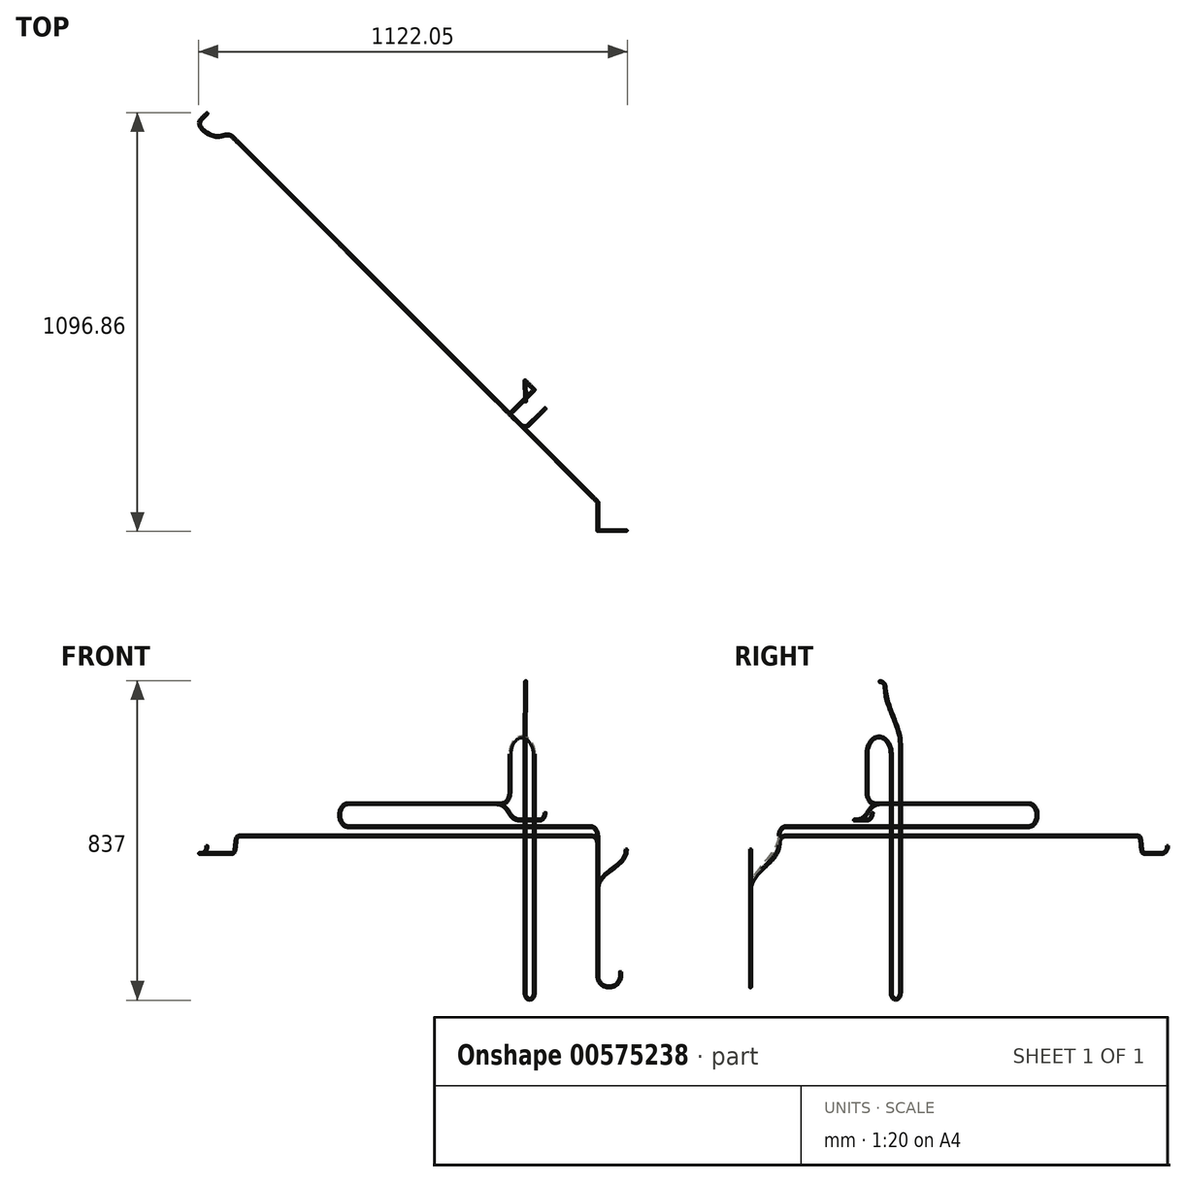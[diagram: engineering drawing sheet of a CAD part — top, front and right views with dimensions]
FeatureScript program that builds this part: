
annotation { "Feature Type Name" : "Feature", "Feature Type Description" : "" }
export const myFeature = defineFeature(function(context is Context, id is Id, definition is map)
    precondition{}
    {
        {
            var Q0;
            Q0=qCreatedBy(makeId("Top.planeOp"),FACE);
            var sketch = newSketch(context, id + "F0", { "sketchPlane" : qUnion([Q0])});
            skCircle(sketch, "E0", {"center": v(0, 0) * mm, "radius": 2.5 * mm});
            skSolve(sketch);
        }
        {
            var Q0;
            Q0=qCreatedBy(makeId("Front.planeOp"),FACE);
            var sketch = newSketch(context, id + "F1", { "sketchPlane" : qUnion([Q0])});
            skLineSegment(sketch, "E1", {"start": v(0, 0) * mm, "end": v(0, -10) * mm});
            skArc(sketch, "E2", {"start": v(-60, -10) * mm, "mid": v(-30, -40) * mm, "end": v(0, -10) * mm});
            skLineSegment(sketch, "E3", {"start": v(-60, -10) * mm, "end": v(-60, 215) * mm});
            skFitSpline(sketch, "E4", {"points": [v(-60, 215) * mm, v(-22.5, 268) * mm, v(15, 321) * mm], "startDerivative": vector(0, 150) * mm, "endDerivative": vector(0, 150) * mm});
            skLineSegment(sketch, "E5", {"start": v(15, 296) * mm, "end": v(15, 321) * mm, "construction": true});
            skLineSegment(sketch, "E6", {"start": v(-60, 240) * mm, "end": v(-60, 215) * mm, "construction": true});
            skLineSegment(sketch, "E7", {"start": v(15, 321) * mm, "end": v(-60, 215) * mm, "construction": true});
            skSolve(sketch);
        }
        {
            var Q0;
            Q0=qSketchRegion(id+"F0",true);
            var Q1;
            Q1=qConstructionFilter(qBodyType(qCreatedBy(id+"F1",EDGE),BodyType.WIRE),ConstructionObject.NO);
            sweep(context, id + "F2", {"profiles" : qUnion([Q0]), "path" : qUnion([Q1])});
        }
        {
            var Q0;
            Q0=qCreatedBy(makeId("Front.planeOp"),FACE);
            var sketch = newSketch(context, id + "F3", { "sketchPlane" : qUnion([Q0])});
            skLineSegment(sketch, "E8", {"start": v(0, 0) * mm, "end": v(0, -10) * mm});
            skArc(sketch, "E9", {"start": v(-60, -10) * mm, "mid": v(-30, -40) * mm, "end": v(0, -10) * mm});
            skLineSegment(sketch, "E10", {"start": v(-60, -10) * mm, "end": v(-60, 215) * mm});
            skSolve(sketch);
        }
        {
            var Q0;
            Q0=qCreatedBy(makeId("Right.planeOp"),FACE);
            var Q1;
            Q1=sQuery(id+"F3.wireOp",VERTEX,"E10.end");
            cPlane(context, id + "F4", {"entities" : qUnion([Q0, Q1]), "cplaneType" : CPlaneType.PLANE_POINT, "offset" : 25 * mm, "width" : 150 * mm, "height" : 150 * mm});
        }
        {
            var Q0;
            Q0=qCreatedBy(id+"F4.planeOp",FACE);
            var sketch = newSketch(context, id + "F5", { "sketchPlane" : qUnion([Q0])});
            skFitSpline(sketch, "E11", {"points": [v(0, 215) * mm, v(37.5, 275) * mm, v(75, 335) * mm], "startDerivative": vector(0, 150) * mm, "endDerivative": vector(0, 150) * mm});
            skLineSegment(sketch, "E12", {"start": v(75, 310) * mm, "end": v(75, 335) * mm, "construction": true});
            skLineSegment(sketch, "E13", {"start": v(0, 240) * mm, "end": v(0, 215) * mm, "construction": true});
            skLineSegment(sketch, "E14", {"start": v(0, 215) * mm, "end": v(75, 335) * mm, "construction": true});
            skSolve(sketch);
        }
        {
            var Q0;
            Q0=sQuery(id+"F5.wireOp",EDGE,"E12");
            cPlane(context, id + "F6", {"entities" : qUnion([Q0]), "cplaneType" : CPlaneType.LINE_ANGLE, "offset" : 25 * mm, "angle" : 135 * degree, "oppositeDirection" : true, "width" : 150 * mm, "height" : 150 * mm});
        }
        {
            var Q0;
            Q0=qCreatedBy(id+"F6.planeOp",FACE);
            var sketch = newSketch(context, id + "F7", { "sketchPlane" : qUnion([Q0])});
            skArc(sketch, "E15", {"start": v(-95.46, 335) * mm, "mid": v(-101.32, 349.14) * mm, "end": v(-115.46, 355) * mm});
            skLineSegment(sketch, "E16", {"start": v(-115.46, 355) * mm, "end": v(-1423.46, 355) * mm});
            skFitSpline(sketch, "E17", {"points": [v(-1423.46, 355) * mm, v(-1435.96, 332.5) * mm, v(-1448.46, 310) * mm], "startDerivative": vector(-60, 0) * mm, "endDerivative": vector(-60, 0) * mm});
            skLineSegment(sketch, "E18", {"start": v(-1433.46, 355) * mm, "end": v(-1423.46, 355) * mm, "construction": true});
            skLineSegment(sketch, "E19", {"start": v(-1438.46, 310) * mm, "end": v(-1448.46, 310) * mm, "construction": true});
            skLineSegment(sketch, "E20", {"start": v(-1448.46, 310) * mm, "end": v(-1423.46, 355) * mm, "construction": true});
            skSolve(sketch);
        }
        {
            var Q0;
            Q0=sQuery(id+"F7.wireOp",EDGE,"E19");
            cPlane(context, id + "F8", {"entities" : qUnion([Q0]), "cplaneType" : CPlaneType.LINE_ANGLE, "offset" : 25 * mm, "angle" : 0 * degree, "width" : 150 * mm, "height" : 150 * mm});
        }
        {
            var Q0;
            Q0=qCreatedBy(id+"F8.planeOp",FACE);
            var sketch = newSketch(context, id + "F9", { "sketchPlane" : qUnion([Q0])});
            skFitSpline(sketch, "E21", {"points": [v(-1016.72, 1031.72) * mm, v(-1061.72, 1032.72) * mm, v(-1096.72, 1077.72) * mm], "startDerivative": vector(-67.63, 67.63) * mm, "endDerivative": vector(100.16, 100.16) * mm});
            skLineSegment(sketch, "E22", {"start": v(-1114.4, 1060.04) * mm, "end": v(-1096.72, 1077.72) * mm, "construction": true});
            skLineSegment(sketch, "E23", {"start": v(-1016.72, 1031.72) * mm, "end": v(-1027.32, 1042.32) * mm, "construction": true});
            skSolve(sketch);
        }
        {
            var Q0;
            Q0=sQuery(id+"F9.wireOp",EDGE,"E22");
            cPlane(context, id + "F10", {"entities" : qUnion([Q0]), "cplaneType" : CPlaneType.LINE_ANGLE, "offset" : 25 * mm, "angle" : 90 * degree, "width" : 150 * mm, "height" : 150 * mm});
        }
        {
            var Q0;
            Q0=qCreatedBy(id+"F10.planeOp",FACE);
            var sketch = newSketch(context, id + "F11", { "sketchPlane" : qUnion([Q0])});
            skArc(sketch, "E24", {"start": v(-13.44, 310) * mm, "mid": v(0.7, 315.86) * mm, "end": v(6.56, 330) * mm});
            skSolve(sketch);
        }
        {
            var Q0;
            Q0=qSketchRegion(id+"F0",true);
            var Q1;
            Q1=qConstructionFilter(qBodyType(qCreatedBy(id+"F3",EDGE),BodyType.WIRE),ConstructionObject.NO);
            var Q2;
            Q2=qConstructionFilter(qBodyType(qCreatedBy(id+"F5",EDGE),BodyType.WIRE),ConstructionObject.NO);
            var Q3;
            Q3=qConstructionFilter(qBodyType(qCreatedBy(id+"F7",EDGE),BodyType.WIRE),ConstructionObject.NO);
            var Q4;
            Q4=qConstructionFilter(qBodyType(qCreatedBy(id+"F9",EDGE),BodyType.WIRE),ConstructionObject.NO);
            var Q5;
            Q5=qConstructionFilter(qBodyType(qCreatedBy(id+"F11",EDGE),BodyType.WIRE),ConstructionObject.NO);
            sweep(context, id + "F12", {"profiles" : qUnion([Q0]), "path" : qUnion([Q1, Q2, Q3, Q4, Q5])});
        }
        {
            var Q0;
            Q0=qCreatedBy(makeId("Front.planeOp"),FACE);
            var sketch = newSketch(context, id + "F13", { "sketchPlane" : qUnion([Q0])});
            skLineSegment(sketch, "E25", {"start": v(0, 0) * mm, "end": v(0, -10) * mm});
            skArc(sketch, "E26", {"start": v(-60, -10) * mm, "mid": v(-30, -40) * mm, "end": v(0, -10) * mm});
            skLineSegment(sketch, "E27", {"start": v(-60, -10) * mm, "end": v(-60, 215) * mm});
            skSolve(sketch);
        }
        {
            var Q0;
            Q0=qCreatedBy(makeId("Right.planeOp"),FACE);
            var Q1;
            Q1=sQuery(id+"F13.wireOp",VERTEX,"E27.end");
            cPlane(context, id + "F14", {"entities" : qUnion([Q0, Q1]), "cplaneType" : CPlaneType.PLANE_POINT, "offset" : 25 * mm, "width" : 150 * mm, "height" : 150 * mm});
        }
        {
            var Q0;
            Q0=qCreatedBy(id+"F14.planeOp",FACE);
            var sketch = newSketch(context, id + "F15", { "sketchPlane" : qUnion([Q0])});
            skFitSpline(sketch, "E28", {"points": [v(0, 215) * mm, v(37.5, 285) * mm, v(75, 355) * mm], "startDerivative": vector(0, 150) * mm, "endDerivative": vector(0, 150) * mm});
            skLineSegment(sketch, "E29", {"start": v(75, 330) * mm, "end": v(75, 355) * mm, "construction": true});
            skLineSegment(sketch, "E30", {"start": v(0, 240) * mm, "end": v(0, 215) * mm, "construction": true});
            skLineSegment(sketch, "E31", {"start": v(0, 215) * mm, "end": v(75, 355) * mm, "construction": true});
            skSolve(sketch);
        }
        {
            var Q0;
            Q0=sQuery(id+"F15.wireOp",EDGE,"E29");
            cPlane(context, id + "F16", {"entities" : qUnion([Q0]), "cplaneType" : CPlaneType.LINE_ANGLE, "offset" : 25 * mm, "angle" : 135 * degree, "oppositeDirection" : true, "width" : 150 * mm, "height" : 150 * mm});
        }
        {
            var Q0;
            Q0=qCreatedBy(id+"F16.planeOp",FACE);
            var sketch = newSketch(context, id + "F17", { "sketchPlane" : qUnion([Q0])});
            skArc(sketch, "E32", {"start": v(-95.46, 355) * mm, "mid": v(-102.78, 372.68) * mm, "end": v(-120.46, 380) * mm});
            skLineSegment(sketch, "E33", {"start": v(-120.46, 380) * mm, "end": v(-1020.46, 380) * mm});
            skArc(sketch, "E34", {"start": v(-1020.46, 440) * mm, "mid": v(-1050.46, 410) * mm, "end": v(-1020.46, 380) * mm});
            skLineSegment(sketch, "E35", {"start": v(-1020.46, 440) * mm, "end": v(-470.46, 440) * mm});
            skFitSpline(sketch, "E36", {"points": [v(-470.46, 440) * mm, v(-425.46, 418.5) * mm, v(-380.46, 397) * mm], "startDerivative": vector(150, 0) * mm, "endDerivative": vector(150, 0) * mm});
            skLineSegment(sketch, "E37", {"start": v(-445.46, 440) * mm, "end": v(-470.46, 440) * mm, "construction": true});
            skLineSegment(sketch, "E38", {"start": v(-405.46, 397) * mm, "end": v(-380.46, 397) * mm, "construction": true});
            skLineSegment(sketch, "E39", {"start": v(-380.46, 397) * mm, "end": v(-470.46, 440) * mm, "construction": true});
            skSolve(sketch);
        }
        {
            var Q0;
            Q0=qCreatedBy(makeId("Top.planeOp"),FACE);
            var Q1;
            Q1=sQuery(id+"F17.wireOp",VERTEX,"E36.end");
            cPlane(context, id + "F18", {"entities" : qUnion([Q0, Q1]), "cplaneType" : CPlaneType.PLANE_POINT, "offset" : 0 * mm, "width" : 150 * mm, "height" : 150 * mm});
        }
        {
            var Q0;
            Q0=qCreatedBy(id+"F18.planeOp",FACE);
            var sketch = newSketch(context, id + "F19", { "sketchPlane" : qUnion([Q0])});
            skArc(sketch, "E40", {"start": v(-261.53, 276.53) * mm, "mid": v(-250.92, 272.13) * mm, "end": v(-240.31, 276.53) * mm});
            skLineSegment(sketch, "E41", {"start": v(-261.53, 276.53) * mm, "end": v(-250.92, 287.13) * mm, "construction": true});
            skLineSegment(sketch, "E42", {"start": v(-240.31, 276.53) * mm, "end": v(-250.92, 287.13) * mm, "construction": true});
            skLineSegment(sketch, "E43", {"start": v(-240.31, 276.53) * mm, "end": v(-212.03, 304.8) * mm});
            skSolve(sketch);
        }
        {
            var Q0;
            Q0=sQuery(id+"F19.wireOp",EDGE,"E43");
            cPlane(context, id + "F20", {"entities" : qUnion([Q0]), "cplaneType" : CPlaneType.LINE_ANGLE, "offset" : 25 * mm, "angle" : 90 * degree, "width" : 150 * mm, "height" : 150 * mm});
        }
        {
            var Q0;
            Q0=qCreatedBy(id+"F20.planeOp",FACE);
            var sketch = newSketch(context, id + "F21", { "sketchPlane" : qUnion([Q0])});
            skArc(sketch, "E44", {"start": v(65.6, 397) * mm, "mid": v(79.75, 402.86) * mm, "end": v(85.6, 417) * mm});
            skSolve(sketch);
        }
        {
            var Q0;
            Q0=qSketchRegion(id+"F0",true);
            var Q1;
            Q1=qConstructionFilter(qBodyType(qCreatedBy(id+"F13",EDGE),BodyType.WIRE),ConstructionObject.NO);
            var Q2;
            Q2=qConstructionFilter(qBodyType(qCreatedBy(id+"F15",EDGE),BodyType.WIRE),ConstructionObject.NO);
            var Q3;
            Q3=qConstructionFilter(qBodyType(qCreatedBy(id+"F17",EDGE),BodyType.WIRE),ConstructionObject.NO);
            var Q4;
            Q4=qConstructionFilter(qBodyType(qCreatedBy(id+"F19",EDGE),BodyType.WIRE),ConstructionObject.NO);
            var Q5;
            Q5=qConstructionFilter(qBodyType(qCreatedBy(id+"F21",EDGE),BodyType.WIRE),ConstructionObject.NO);
            sweep(context, id + "F22", {"profiles" : qUnion([Q0]), "path" : qUnion([Q1, Q2, Q3, Q4, Q5])});
        }
        {
            var Q0;
            Q0=qCreatedBy(makeId("Front.planeOp"),FACE);
            var sketch = newSketch(context, id + "F23", { "sketchPlane" : qUnion([Q0])});
            skLineSegment(sketch, "E45", {"start": v(0, 0) * mm, "end": v(0, -10) * mm});
            skArc(sketch, "E46", {"start": v(-60, -10) * mm, "mid": v(-30, -40) * mm, "end": v(0, -10) * mm});
            skLineSegment(sketch, "E47", {"start": v(-60, -10) * mm, "end": v(-60, 215) * mm});
            skSolve(sketch);
        }
        {
            var Q0;
            Q0=qCreatedBy(makeId("Right.planeOp"),FACE);
            var Q1;
            Q1=sQuery(id+"F23.wireOp",VERTEX,"E47.end");
            cPlane(context, id + "F24", {"entities" : qUnion([Q0, Q1]), "cplaneType" : CPlaneType.PLANE_POINT, "offset" : 25 * mm, "width" : 150 * mm, "height" : 150 * mm});
        }
        {
            var Q0;
            Q0=qCreatedBy(id+"F24.planeOp",FACE);
            var sketch = newSketch(context, id + "F25", { "sketchPlane" : qUnion([Q0])});
            skFitSpline(sketch, "E48", {"points": [v(0, 215) * mm, v(37.5, 285) * mm, v(75, 355) * mm], "startDerivative": vector(0, 150) * mm, "endDerivative": vector(0, 150) * mm});
            skLineSegment(sketch, "E49", {"start": v(75, 330) * mm, "end": v(75, 355) * mm, "construction": true});
            skLineSegment(sketch, "E50", {"start": v(0, 240) * mm, "end": v(0, 215) * mm, "construction": true});
            skLineSegment(sketch, "E51", {"start": v(0, 215) * mm, "end": v(75, 355) * mm, "construction": true});
            skSolve(sketch);
        }
        {
            var Q0;
            Q0=sQuery(id+"F25.wireOp",EDGE,"E49");
            cPlane(context, id + "F26", {"entities" : qUnion([Q0]), "cplaneType" : CPlaneType.LINE_ANGLE, "offset" : 25 * mm, "angle" : 135 * degree, "oppositeDirection" : true, "width" : 150 * mm, "height" : 150 * mm});
        }
        {
            var Q0;
            Q0=qCreatedBy(id+"F26.planeOp",FACE);
            var sketch = newSketch(context, id + "F27", { "sketchPlane" : qUnion([Q0])});
            skArc(sketch, "E52", {"start": v(-95.46, 355) * mm, "mid": v(-102.78, 372.68) * mm, "end": v(-120.46, 380) * mm});
            skLineSegment(sketch, "E53", {"start": v(-120.46, 380) * mm, "end": v(-1020.46, 380) * mm});
            skArc(sketch, "E54", {"start": v(-1020.46, 440) * mm, "mid": v(-1050.46, 410) * mm, "end": v(-1020.46, 380) * mm});
            skLineSegment(sketch, "E55", {"start": v(-1020.46, 440) * mm, "end": v(-450.46, 440) * mm});
            skArc(sketch, "E56", {"start": v(-450.46, 440) * mm, "mid": v(-429.25, 448.79) * mm, "end": v(-420.46, 470) * mm});
            skLineSegment(sketch, "E57", {"start": v(-420.46, 470) * mm, "end": v(-420.46, 428.68) * mm, "construction": true});
            skSolve(sketch);
        }
        {
            var Q0;
            Q0=makeQuery(id+"F34.opSweep","CAP_EDGE",EDGE,{"disambiguationData":[OSD([sQuery(id+"F0.wireOp",EDGE,"E0"),sQuery(id+"F27.wireOp",VERTEX,"E56.end")])],"isStart":false});
            var Q1;
            Q1=sQuery(id+"F27.wireOp",EDGE,"E57");
            cPlane(context, id + "F28", {"entities" : qUnion([Q0, Q1]), "cplaneType" : CPlaneType.LINE_ANGLE, "offset" : 25 * mm, "angle" : 45 * degree, "width" : 150 * mm, "height" : 150 * mm});
        }
        {
            var Q0;
            Q0=qCreatedBy(id+"F28.planeOp",FACE);
            var sketch = newSketch(context, id + "F29", { "sketchPlane" : qUnion([Q0])});
            skLineSegment(sketch, "E58", {"start": v(-10.6, 470) * mm, "end": v(-10.6, 570) * mm});
            skArc(sketch, "E59", {"start": v(-10.6, 570) * mm, "mid": v(-55.6, 615) * mm, "end": v(-100.6, 570) * mm});
            skLineSegment(sketch, "E60", {"start": v(-100.6, 570) * mm, "end": v(-100.6, -55) * mm});
            skSolve(sketch);
        }
        {
            var Q0;
            Q0=sQuery(id+"F29.wireOp",EDGE,"E60");
            cPlane(context, id + "F30", {"entities" : qUnion([Q0]), "cplaneType" : CPlaneType.LINE_ANGLE, "offset" : 25 * mm, "angle" : 225 * degree, "oppositeDirection" : true, "width" : 150 * mm, "height" : 150 * mm});
        }
        {
            var Q0;
            Q0=qCreatedBy(id+"F30.planeOp",FACE);
            var sketch = newSketch(context, id + "F31", { "sketchPlane" : qUnion([Q0])});
            skLineSegment(sketch, "E61", {"start": v(454.46, -55) * mm, "end": v(454.46, 595) * mm});
            skArc(sketch, "E62", {"start": v(420.46, -55) * mm, "mid": v(437.46, -72) * mm, "end": v(454.46, -55) * mm});
            skSolve(sketch);
        }
        {
            var Q0;
            Q0=sQuery(id+"F31.wireOp",EDGE,"E61");
            cPlane(context, id + "F32", {"entities" : qUnion([Q0]), "cplaneType" : CPlaneType.LINE_ANGLE, "offset" : 25 * mm, "angle" : 2 * degree, "width" : 150 * mm, "height" : 150 * mm});
        }
        {
            var Q0;
            Q0=qCreatedBy(id+"F32.planeOp",FACE);
            var sketch = newSketch(context, id + "F33", { "sketchPlane" : qUnion([Q0])});
            skFitSpline(sketch, "E63", {"points": [v(400.98, 595) * mm, v(380.98, 670) * mm, v(360.98, 745) * mm], "startDerivative": vector(0, 150) * mm, "endDerivative": vector(0, 150) * mm});
            skLineSegment(sketch, "E64", {"start": v(400.98, 620) * mm, "end": v(400.98, 595) * mm, "construction": true});
            skLineSegment(sketch, "E65", {"start": v(360.98, 720) * mm, "end": v(360.98, 745) * mm, "construction": true});
            skLineSegment(sketch, "E66", {"start": v(360.98, 745) * mm, "end": v(400.98, 595) * mm, "construction": true});
            skArc(sketch, "E67", {"start": v(360.98, 745) * mm, "mid": v(356.6, 755.6) * mm, "end": v(345.98, 760) * mm});
            skSolve(sketch);
        }
        {
            var Q0;
            Q0=qSketchRegion(id+"F0",true);
            var Q1;
            Q1=qConstructionFilter(qBodyType(qCreatedBy(id+"F23",EDGE),BodyType.WIRE),ConstructionObject.NO);
            var Q2;
            Q2=qConstructionFilter(qBodyType(qCreatedBy(id+"F25",EDGE),BodyType.WIRE),ConstructionObject.NO);
            var Q3;
            Q3=qConstructionFilter(qBodyType(qCreatedBy(id+"F27",EDGE),BodyType.WIRE),ConstructionObject.NO);
            var Q4;
            Q4=qConstructionFilter(qBodyType(qCreatedBy(id+"F29",EDGE),BodyType.WIRE),ConstructionObject.NO);
            var Q5;
            Q5=qConstructionFilter(qBodyType(qCreatedBy(id+"F31",EDGE),BodyType.WIRE),ConstructionObject.NO);
            var Q6;
            Q6=qConstructionFilter(qBodyType(qCreatedBy(id+"F33",EDGE),BodyType.WIRE),ConstructionObject.NO);
            sweep(context, id + "F34", {"profiles" : qUnion([Q0]), "path" : qUnion([Q1, Q2, Q3, Q4, Q5, Q6])});
        }
        {
            var Q0;
            Q0=qSketchRegion(id+"F0",true);
            var Q1;
            Q1=sQuery(id+"F23.wireOp",EDGE,"E45");
            var Q2;
            Q2=sQuery(id+"F23.wireOp",EDGE,"E46");
            var Q3;
            Q3=sQuery(id+"F23.wireOp",EDGE,"E47");
            var Q4;
            Q4=sQuery(id+"F25.wireOp",EDGE,"E48");
            var Q5;
            Q5=sQuery(id+"F27.wireOp",EDGE,"E52");
            var Q6;
            Q6=sQuery(id+"F27.wireOp",EDGE,"E53");
            var Q7;
            Q7=sQuery(id+"F27.wireOp",EDGE,"E54");
            var Q8;
            Q8=sQuery(id+"F27.wireOp",EDGE,"E55");
            var Q9;
            Q9=sQuery(id+"F27.wireOp",EDGE,"E56");
            var Q10;
            Q10=qConstructionFilter(qBodyType(qCreatedBy(id+"F29",EDGE),BodyType.WIRE),ConstructionObject.NO);
            sweep(context, id + "F35", {"profiles" : qUnion([Q0]), "path" : qUnion([Q1, Q2, Q3, Q4, Q5, Q6, Q7, Q8, Q9, Q10])});
        }
    });
